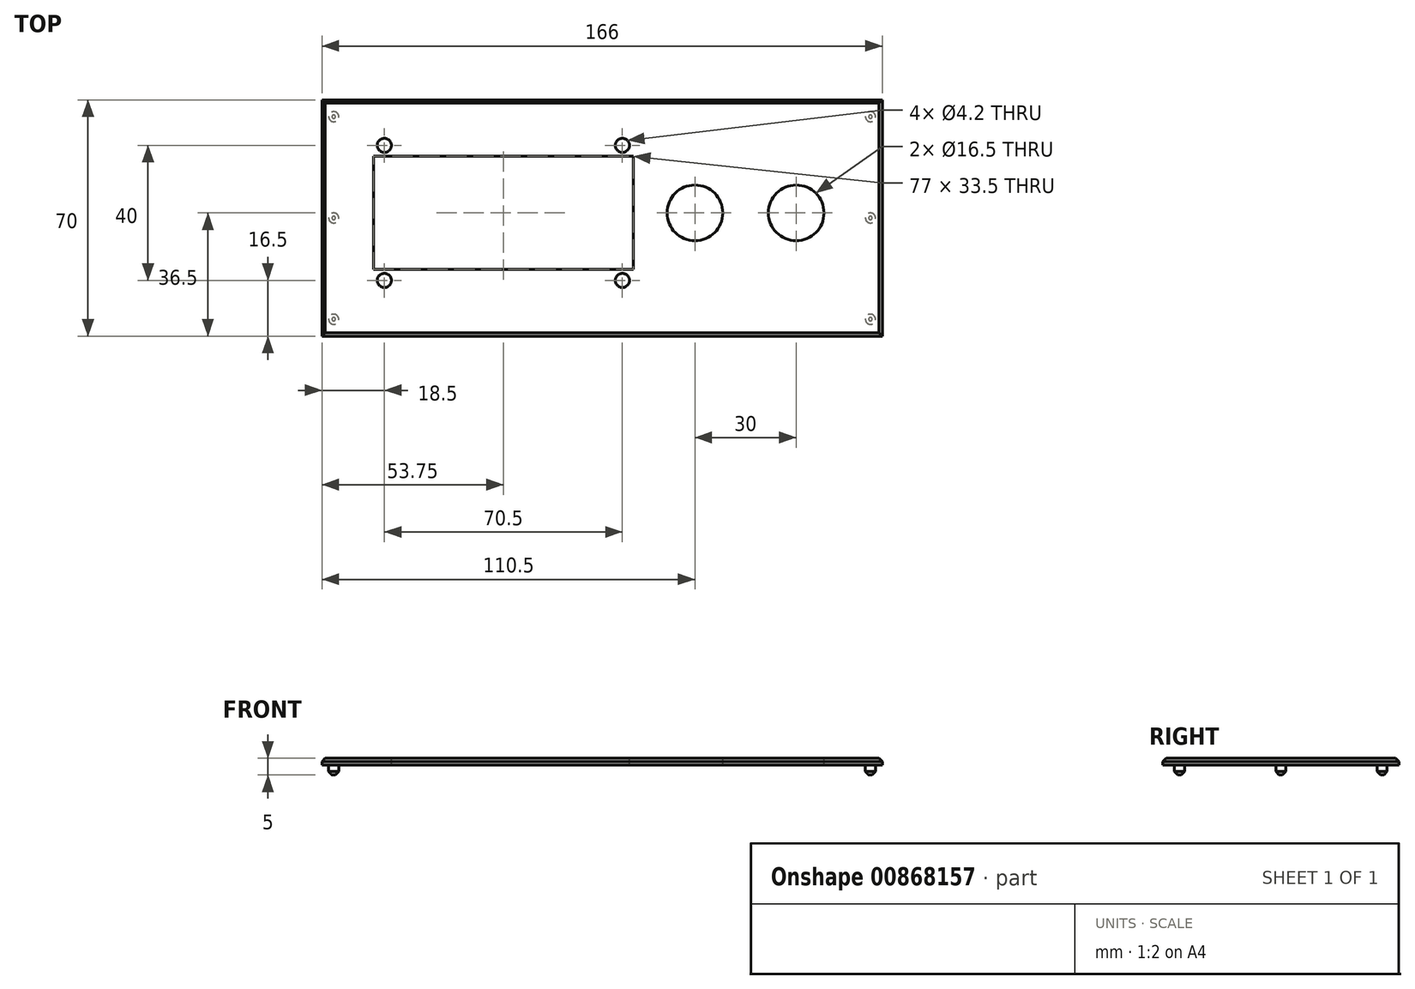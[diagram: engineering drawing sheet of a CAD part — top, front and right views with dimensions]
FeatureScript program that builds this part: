
annotation { "Feature Type Name" : "Feature", "Feature Type Description" : "" }
export const myFeature = defineFeature(function(context is Context, id is Id, definition is map)
    precondition{}
    {
        {
            var Q0;
            Q0=qCreatedBy(makeId("Top.planeOp"),FACE);
            var sketch = newSketch(context, id + "F0", { "sketchPlane" : qUnion([Q0])});
            skLineSegment(sketch, "E0.bottom", {"start": v(-83, 35) * mm, "end": v(83, 35) * mm});
            skLineSegment(sketch, "E0.top", {"start": v(-83, -35) * mm, "end": v(83, -35) * mm});
            skLineSegment(sketch, "E0.left", {"start": v(-83, 35) * mm, "end": v(-83, -35) * mm});
            skLineSegment(sketch, "E0.right", {"start": v(83, 35) * mm, "end": v(83, -35) * mm});
            skLineSegment(sketch, "E1", {"start": v(-83, -35) * mm, "end": v(83, 35) * mm, "construction": true});
            skSolve(sketch);
        }
        {
            var Q0;
            Q0 = qSketchRegion(id + "F0", true);
            extrude(context, id + "F1", {"entities" : qUnion([Q0]), "depth" : 2 * mm, "offsetDistance" : 25 * mm});
        }
        {
            var Q0;
            Q0=makeQuery(id+"F1.opExtrude","CAP_FACE",FACE,{"disambiguationData":[OSD([sQuery(id+"F0.wireOp",EDGE,"E0.bottom"),sQuery(id+"F0.wireOp",EDGE,"E0.top"),sQuery(id+"F0.wireOp",EDGE,"E0.left"),sQuery(id+"F0.wireOp",EDGE,"E0.right")])],"isStart":false});
            var sketch = newSketch(context, id + "F2", { "sketchPlane" : qUnion([Q0])});
            skLineSegment(sketch, "E2.bottom", {"start": v(-67.75, 18.25) * mm, "end": v(9.25, 18.25) * mm});
            skLineSegment(sketch, "E2.top", {"start": v(-67.75, -15.25) * mm, "end": v(9.25, -15.25) * mm});
            skLineSegment(sketch, "E2.left", {"start": v(-67.75, 18.25) * mm, "end": v(-67.75, -15.25) * mm});
            skLineSegment(sketch, "E2.right", {"start": v(9.25, 18.25) * mm, "end": v(9.25, -15.25) * mm});
            skLineSegment(sketch, "E3.bottom", {"start": v(-68, 25) * mm, "end": v(9.5, 25) * mm, "construction": true});
            skLineSegment(sketch, "E3.top", {"start": v(-68, -22) * mm, "end": v(9.5, -22) * mm, "construction": true});
            skLineSegment(sketch, "E3.left", {"start": v(-68, 25) * mm, "end": v(-68, -22) * mm, "construction": true});
            skLineSegment(sketch, "E3.right", {"start": v(9.5, 25) * mm, "end": v(9.5, -22) * mm, "construction": true});
            skCircle(sketch, "E4", {"center": v(-64.5, 21.5) * mm, "radius": 2.1 * mm});
            skLineSegment(sketch, "E5", {"start": v(-68, 1.5) * mm, "end": v(83, 1.5) * mm, "construction": true});
            skLineSegment(sketch, "E6", {"start": v(-29.25, 25) * mm, "end": v(-29.25, -22) * mm, "construction": true});
            skCircle(sketch, "E7.MirrorC", {"center": v(6, 21.5) * mm, "radius": 2.1 * mm});
            skCircle(sketch, "E8.MirrorC", {"center": v(6, -18.5) * mm, "radius": 2.1 * mm});
            skCircle(sketch, "E9.MirrorC", {"center": v(-64.5, -18.5) * mm, "radius": 2.1 * mm});
            skCircle(sketch, "E10", {"center": v(27.5, 1.5) * mm, "radius": 8.25 * mm});
            skCircle(sketch, "E11", {"center": v(27.5, 1.5) * mm, "radius": 12.5 * mm, "construction": true});
            skCircle(sketch, "E12", {"center": v(57.5, 1.5) * mm, "radius": 8.25 * mm});
            skCircle(sketch, "E13", {"center": v(57.5, 1.5) * mm, "radius": 12.5 * mm, "construction": true});
            skSolve(sketch);
        }
        {
            var Q0;
            Q0 = qSketchRegion(id + "F2", true);
            var Q1;
            Q1=makeQuery(id+"F1.opExtrude","CAP_FACE",FACE,{"disambiguationData":[OSD([sQuery(id+"F0.wireOp",EDGE,"E0.bottom"),sQuery(id+"F0.wireOp",EDGE,"E0.top"),sQuery(id+"F0.wireOp",EDGE,"E0.left"),sQuery(id+"F0.wireOp",EDGE,"E0.right")])],"isStart":true});
            extrude(context, id + "F3", {"entities" : qUnion([Q0]), "operationType" : NewBodyOperationType.REMOVE, "endBound" : BoundingType.UP_TO_SURFACE, "oppositeDirection" : true, "depth" : 25 * mm, "endBoundEntityFace" : qUnion([Q1]), "offsetDistance" : 25 * mm});
        }
        {
            var Q0;
            Q0=makeQuery(id+"F1.opExtrude","CAP_FACE",FACE,{"disambiguationData":[OSD([sQuery(id+"F0.wireOp",EDGE,"E0.bottom"),sQuery(id+"F0.wireOp",EDGE,"E0.top"),sQuery(id+"F0.wireOp",EDGE,"E0.left"),sQuery(id+"F0.wireOp",EDGE,"E0.right")])],"isStart":true});
            var sketch = newSketch(context, id + "F4", { "sketchPlane" : qUnion([Q0])});
            skCircle(sketch, "E14", {"center": v(-79.5, 30) * mm, "radius": 1.5 * mm});
            skCircle(sketch, "E15.MirrorC", {"center": v(-79.5, -30) * mm, "radius": 1.5 * mm});
            skCircle(sketch, "E16", {"center": v(-79.5, 0) * mm, "radius": 1.5 * mm});
            skLineSegment(sketch, "E17", {"start": v(-79.5, 30) * mm, "end": v(-79.5, -30) * mm, "construction": true});
            skCircle(sketch, "E18.MirrorC", {"center": v(79.5, -30) * mm, "radius": 1.5 * mm});
            skCircle(sketch, "E19.MirrorC", {"center": v(79.5, 30) * mm, "radius": 1.5 * mm});
            skCircle(sketch, "E20.MirrorC", {"center": v(79.5, 0) * mm, "radius": 1.5 * mm});
            skSolve(sketch);
        }
        {
            var Q0;
            Q0 = qSketchRegion(id + "F4", true);
            extrude(context, id + "F5", {"entities" : qUnion([Q0]), "operationType" : NewBodyOperationType.ADD, "depth" : 3 * mm, "offsetDistance" : 25 * mm});
        }
        {
            var Q0;
            Q0=makeQuery(id+"F5.opExtrude","CAP_EDGE",EDGE,{"disambiguationData":[OSD([sQuery(id+"F4.wireOp",EDGE,"E14")])],"isStart":false});
            var Q1;
            Q1=makeQuery(id+"F5.opExtrude","CAP_EDGE",EDGE,{"disambiguationData":[OSD([sQuery(id+"F4.wireOp",EDGE,"E16")])],"isStart":false});
            var Q2;
            Q2=makeQuery(id+"F5.opExtrude","CAP_EDGE",EDGE,{"disambiguationData":[OSD([sQuery(id+"F4.wireOp",EDGE,"E15.MirrorC")])],"isStart":false});
            var Q3;
            Q3=makeQuery(id+"F5.opExtrude","CAP_EDGE",EDGE,{"disambiguationData":[OSD([sQuery(id+"F4.wireOp",EDGE,"E18.MirrorC")])],"isStart":false});
            var Q4;
            Q4=makeQuery(id+"F5.opExtrude","CAP_EDGE",EDGE,{"disambiguationData":[OSD([sQuery(id+"F4.wireOp",EDGE,"E20.MirrorC")])],"isStart":false});
            var Q5;
            Q5=makeQuery(id+"F5.opExtrude","CAP_EDGE",EDGE,{"disambiguationData":[OSD([sQuery(id+"F4.wireOp",EDGE,"E19.MirrorC")])],"isStart":false});
            chamfer(context, id + "F6", {"entities" : qUnion([Q0, Q1, Q2, Q3, Q4, Q5]), "width" : 1 * mm, "tangentPropagation" : true});
        }
        {
            var Q0;
            Q0=makeQuery(id+"F1.opExtrude","CAP_EDGE",EDGE,{"disambiguationData":[OSD([sQuery(id+"F0.wireOp",EDGE,"E0.right")])],"isStart":false});
            var Q1;
            Q1=makeQuery(id+"F1.opExtrude","CAP_EDGE",EDGE,{"disambiguationData":[OSD([sQuery(id+"F0.wireOp",EDGE,"E0.top")])],"isStart":false});
            var Q2;
            Q2=makeQuery(id+"F1.opExtrude","CAP_EDGE",EDGE,{"disambiguationData":[OSD([sQuery(id+"F0.wireOp",EDGE,"E0.left")])],"isStart":false});
            var Q3;
            Q3=makeQuery(id+"F1.opExtrude","CAP_EDGE",EDGE,{"disambiguationData":[OSD([sQuery(id+"F0.wireOp",EDGE,"E0.bottom")])],"isStart":false});
            chamfer(context, id + "F7", {"entities" : qUnion([Q0, Q1, Q2, Q3]), "width" : 1 * mm, "tangentPropagation" : true});
        }
    });
